# Revit family: Sink-Top_Mount-Kitchen-KOHLER-BALLAD-K-3268T
name_source: partatom
category: Plumbing Fixtures
revit_build: Autodesk Revit 2017 (Build: 20160225_1515(x64)
units: mm (PartAtom-declared; Revit-internal decimal feet)

## family parameters
Cut with Voids When Loaded = No
Host = Face
OmniClass Number = 23.31.13.00
OmniClass Title = Sinks
Part Type = Normal
Room Calculation Point = No
Round Connector Dimension = Use Diameter
Shared = No

## types (4) — shared parameters
ADA Compliant = No
Assembly Code = D2010400
CW Connection = No
Cold Water Inlet = Cold Water Inlet
Date Modified = 11/02/2020
Default Elevation = 36"
Description = Over-the-counter kitchen basin
Drain Included = Yes
HW Connection = No
Height = 10 15/16"
Hot Water Inlet = Hot Water Inlet
Length = 18 1/2"
Manufacturer = KOHLER Co.
Master Format 2014 = 22 41 16
Master Format 2014 Name = Residential Lavatories and Sinks
Material = STAINLESS STEEL
Product Documentation Link = https://files.kohler.com.cn
Product Name = BALLAD
Product Page URL = https://www.kohler.com.cn
URL = http://www.kohler.com.cn
Vent Connection = No
Waste Connection = Yes
Waste Water Outlet 1 = Waste Water Outlet 1
Waste Water Outlet 2 = Waste Water Outlet 2
WaterSense Certified = No
Width = 33 1/16"

## per-type parameters (varying)
| type | Finish | Model | Type |
| 2KD, NA-Stainless Steel | Kohler-Metal-NA-Stainless_Steel_Wire_Drawing | K-3268T-2KD-NA | 1 |
| 2KD, KS-Pearl Silver | Kohler-Metal-KS-Pearl_Silver | K-3268T-2KD-KS | 2 |
| 2FD, NA-Stainless Steel | Kohler-Metal-NA-Stainless_Steel_Wire_Drawing | K-3268T-2FD-NA | 3 |
| 2FD, AKF-Pearl Silver | Kohler-Metal-AKF-Pearl_Silver | K-3268T-2FD-AKF | 4 |

## geometry (parser evidence)
native form markers: Sweep x7
no freeform markers — native parametric forms only
